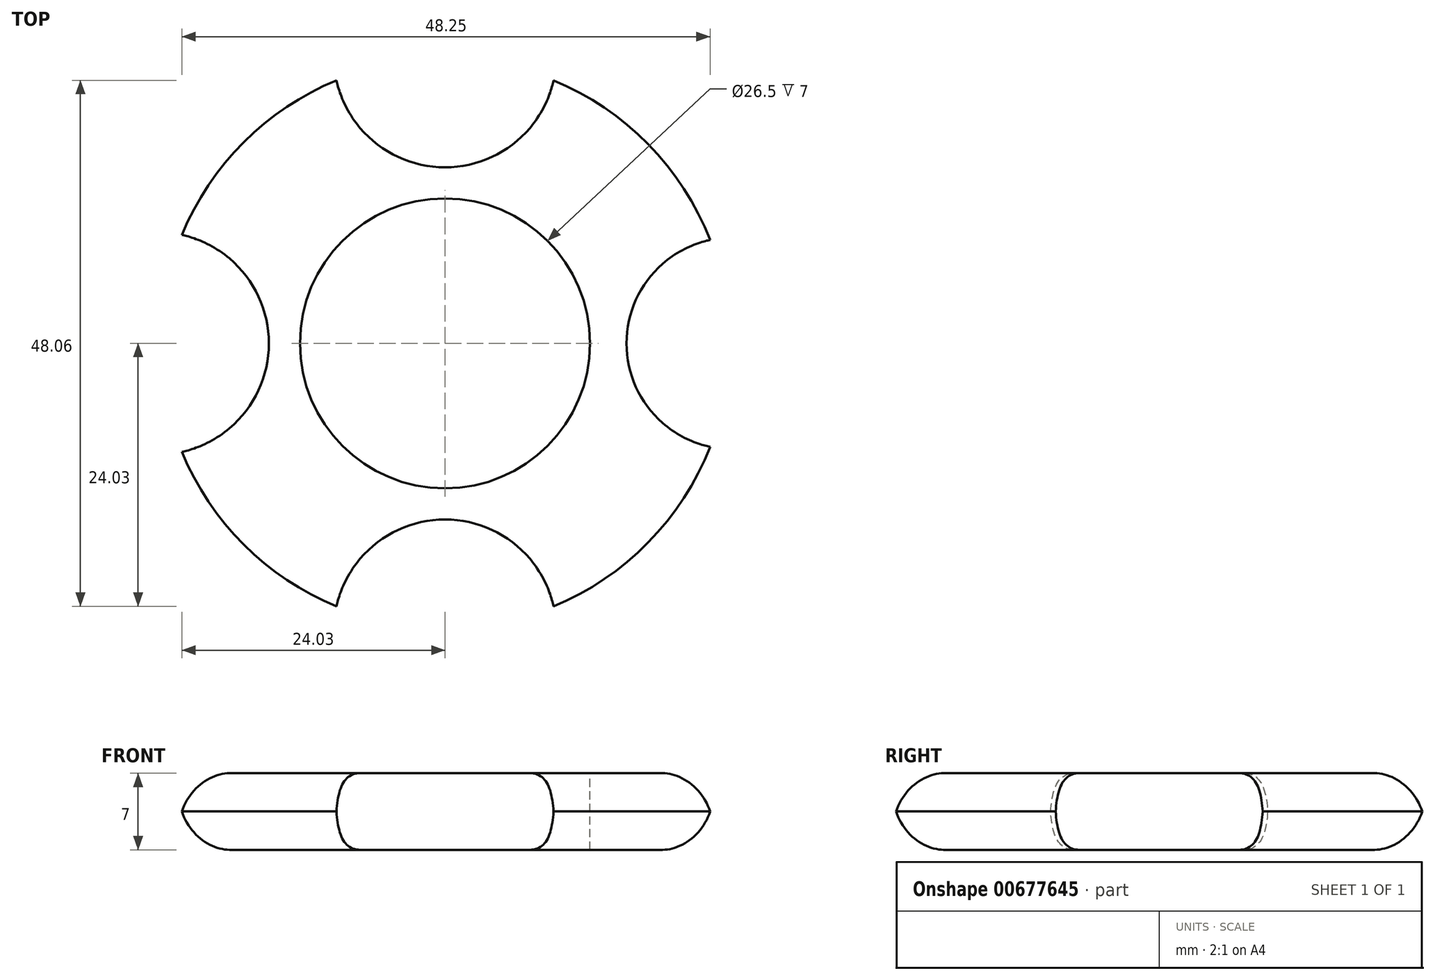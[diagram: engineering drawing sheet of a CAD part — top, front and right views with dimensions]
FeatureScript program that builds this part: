
annotation { "Feature Type Name" : "Feature", "Feature Type Description" : "" }
export const myFeature = defineFeature(function(context is Context, id is Id, definition is map)
    precondition{}
    {
        {
            var Q0;
            Q0=qCreatedBy(makeId("Top.planeOp"),FACE);
            var sketch = newSketch(context, id + "F0", { "sketchPlane" : qUnion([Q0])});
            skCircle(sketch, "E0", {"center": v(0, 0) * mm, "radius": 26.25 * mm});
            skSolve(sketch);
        }
        {
            var Q0;
            Q0=qSketchRegion(id+"F0",true);
            extrude(context, id + "F1", {"entities" : qUnion([Q0]), "depth" : 7 * mm, "offsetDistance" : 25.4 * mm});
        }
        {
            var Q0;
            Q0=makeQuery(id+"F1.opExtrude","CAP_FACE",FACE,{"disambiguationData":[OSD([sQuery(id+"F0.wireOp",EDGE,"E0")])],"isStart":false});
            var sketch = newSketch(context, id + "F2", { "sketchPlane" : qUnion([Q0])});
            skCircle(sketch, "E1", {"center": v(0, 0) * mm, "radius": 13.25 * mm});
            skSolve(sketch);
        }
        {
            var Q0;
            Q0=qSketchRegion(id+"F2",true);
            extrude(context, id + "F3", {"entities" : qUnion([Q0]), "operationType" : NewBodyOperationType.REMOVE, "oppositeDirection" : true, "depth" : 25.4 * mm, "offsetDistance" : 25.4 * mm});
        }
        {
            var Q0;
            Q0=makeQuery(id+"F1.opExtrude","CAP_FACE",FACE,{"disambiguationData":[OSD([sQuery(id+"F0.wireOp",EDGE,"E0")])],"isStart":false});
            var sketch = newSketch(context, id + "F4", { "sketchPlane" : qUnion([Q0])});
            skCircle(sketch, "E2", {"center": v(0, -26.25) * mm, "radius": 10.16 * mm});
            skCircle(sketch, "E3", {"center": v(-26.25, 0) * mm, "radius": 10.16 * mm});
            skCircle(sketch, "E4", {"center": v(0, 26.25) * mm, "radius": 10.16 * mm});
            skCircle(sketch, "E5", {"center": v(26.25, 0) * mm, "radius": 9.67 * mm});
            skSolve(sketch);
        }
        {
            var Q0;
            Q0=qSketchRegion(id+"F4",true);
            extrude(context, id + "F5", {"entities" : qUnion([Q0]), "operationType" : NewBodyOperationType.REMOVE, "oppositeDirection" : true, "depth" : 25.4 * mm, "offsetDistance" : 25.4 * mm});
        }
        {
            var Q0;
            {var subQ0=sQuery(id+"F0.wireOp",EDGE,"E0");Q0=makeQuery(id+"F5.boolean.opBoolean","SPLIT",EDGE,{"disambiguationData":[TD([makeQuery(id+"F1.opExtrude","SWEPT_FACE",FACE,{"disambiguationData":[OSD([subQ0])]}),makeQuery(id+"F1.opExtrude","CAP_FACE",FACE,{"disambiguationData":[OSD([subQ0])],"isStart":true}),makeQuery(id+"F5.opExtrude","SWEPT_FACE",FACE,{"disambiguationData":[OSD([sQuery(id+"F4.wireOp",EDGE,"E2")])]}),makeQuery(id+"F5.opExtrude","SWEPT_FACE",FACE,{"disambiguationData":[OSD([sQuery(id+"F4.wireOp",EDGE,"E5")])]})])],"derivedFrom":makeQuery(id+"F1.opExtrude","CAP_EDGE",EDGE,{"disambiguationData":[OSD([subQ0])],"isStart":true})});}
            var Q1;
            {var subQ0=sQuery(id+"F0.wireOp",EDGE,"E0");Q1=makeQuery(id+"F5.boolean.opBoolean","SPLIT",EDGE,{"disambiguationData":[TD([makeQuery(id+"F1.opExtrude","SWEPT_FACE",FACE,{"disambiguationData":[OSD([subQ0])]}),makeQuery(id+"F1.opExtrude","CAP_FACE",FACE,{"disambiguationData":[OSD([subQ0])],"isStart":true}),makeQuery(id+"F5.opExtrude","SWEPT_FACE",FACE,{"disambiguationData":[OSD([sQuery(id+"F4.wireOp",EDGE,"E2")])]}),makeQuery(id+"F5.opExtrude","SWEPT_FACE",FACE,{"disambiguationData":[OSD([sQuery(id+"F4.wireOp",EDGE,"E3")])]})])],"derivedFrom":makeQuery(id+"F1.opExtrude","CAP_EDGE",EDGE,{"disambiguationData":[OSD([subQ0])],"isStart":true})});}
            var Q2;
            {var subQ0=sQuery(id+"F0.wireOp",EDGE,"E0");Q2=makeQuery(id+"F5.boolean.opBoolean","SPLIT",EDGE,{"disambiguationData":[TD([makeQuery(id+"F1.opExtrude","SWEPT_FACE",FACE,{"disambiguationData":[OSD([subQ0])]}),makeQuery(id+"F1.opExtrude","CAP_FACE",FACE,{"disambiguationData":[OSD([subQ0])],"isStart":true}),makeQuery(id+"F5.opExtrude","SWEPT_FACE",FACE,{"disambiguationData":[OSD([sQuery(id+"F4.wireOp",EDGE,"E3")])]}),makeQuery(id+"F5.opExtrude","SWEPT_FACE",FACE,{"disambiguationData":[OSD([sQuery(id+"F4.wireOp",EDGE,"E4")])]})])],"derivedFrom":makeQuery(id+"F1.opExtrude","CAP_EDGE",EDGE,{"disambiguationData":[OSD([subQ0])],"isStart":true})});}
            var Q3;
            {var subQ0=sQuery(id+"F0.wireOp",EDGE,"E0");Q3=makeQuery(id+"F5.boolean.opBoolean","SPLIT",EDGE,{"disambiguationData":[TD([makeQuery(id+"F1.opExtrude","SWEPT_FACE",FACE,{"disambiguationData":[OSD([subQ0])]}),makeQuery(id+"F1.opExtrude","CAP_FACE",FACE,{"disambiguationData":[OSD([subQ0])],"isStart":false}),makeQuery(id+"F5.opExtrude","SWEPT_FACE",FACE,{"disambiguationData":[OSD([sQuery(id+"F4.wireOp",EDGE,"E3")])]}),makeQuery(id+"F5.opExtrude","SWEPT_FACE",FACE,{"disambiguationData":[OSD([sQuery(id+"F4.wireOp",EDGE,"E4")])]})])],"derivedFrom":makeQuery(id+"F1.opExtrude","CAP_EDGE",EDGE,{"disambiguationData":[OSD([subQ0])],"isStart":false})});}
            var Q4;
            {var subQ0=sQuery(id+"F0.wireOp",EDGE,"E0");Q4=makeQuery(id+"F5.boolean.opBoolean","SPLIT",EDGE,{"disambiguationData":[TD([makeQuery(id+"F1.opExtrude","SWEPT_FACE",FACE,{"disambiguationData":[OSD([subQ0])]}),makeQuery(id+"F1.opExtrude","CAP_FACE",FACE,{"disambiguationData":[OSD([subQ0])],"isStart":false}),makeQuery(id+"F5.opExtrude","SWEPT_FACE",FACE,{"disambiguationData":[OSD([sQuery(id+"F4.wireOp",EDGE,"E2")])]}),makeQuery(id+"F5.opExtrude","SWEPT_FACE",FACE,{"disambiguationData":[OSD([sQuery(id+"F4.wireOp",EDGE,"E3")])]})])],"derivedFrom":makeQuery(id+"F1.opExtrude","CAP_EDGE",EDGE,{"disambiguationData":[OSD([subQ0])],"isStart":false})});}
            var Q5;
            {var subQ0=sQuery(id+"F0.wireOp",EDGE,"E0");Q5=makeQuery(id+"F5.boolean.opBoolean","SPLIT",EDGE,{"disambiguationData":[TD([makeQuery(id+"F1.opExtrude","SWEPT_FACE",FACE,{"disambiguationData":[OSD([subQ0])]}),makeQuery(id+"F1.opExtrude","CAP_FACE",FACE,{"disambiguationData":[OSD([subQ0])],"isStart":false}),makeQuery(id+"F5.opExtrude","SWEPT_FACE",FACE,{"disambiguationData":[OSD([sQuery(id+"F4.wireOp",EDGE,"E2")])]}),makeQuery(id+"F5.opExtrude","SWEPT_FACE",FACE,{"disambiguationData":[OSD([sQuery(id+"F4.wireOp",EDGE,"E5")])]})])],"derivedFrom":makeQuery(id+"F1.opExtrude","CAP_EDGE",EDGE,{"disambiguationData":[OSD([subQ0])],"isStart":false})});}
            var Q6;
            {var subQ0=sQuery(id+"F0.wireOp",EDGE,"E0");Q6=makeQuery(id+"F5.boolean.opBoolean","SPLIT",EDGE,{"disambiguationData":[TD([makeQuery(id+"F1.opExtrude","SWEPT_FACE",FACE,{"disambiguationData":[OSD([subQ0])]}),makeQuery(id+"F1.opExtrude","CAP_FACE",FACE,{"disambiguationData":[OSD([subQ0])],"isStart":false}),makeQuery(id+"F5.opExtrude","SWEPT_FACE",FACE,{"disambiguationData":[OSD([sQuery(id+"F4.wireOp",EDGE,"E4")])]}),makeQuery(id+"F5.opExtrude","SWEPT_FACE",FACE,{"disambiguationData":[OSD([sQuery(id+"F4.wireOp",EDGE,"E5")])]})])],"derivedFrom":makeQuery(id+"F1.opExtrude","CAP_EDGE",EDGE,{"disambiguationData":[OSD([subQ0])],"isStart":false})});}
            var Q7;
            {var subQ0=sQuery(id+"F0.wireOp",EDGE,"E0");Q7=makeQuery(id+"F5.boolean.opBoolean","SPLIT",EDGE,{"disambiguationData":[TD([makeQuery(id+"F1.opExtrude","SWEPT_FACE",FACE,{"disambiguationData":[OSD([subQ0])]}),makeQuery(id+"F1.opExtrude","CAP_FACE",FACE,{"disambiguationData":[OSD([subQ0])],"isStart":true}),makeQuery(id+"F5.opExtrude","SWEPT_FACE",FACE,{"disambiguationData":[OSD([sQuery(id+"F4.wireOp",EDGE,"E4")])]}),makeQuery(id+"F5.opExtrude","SWEPT_FACE",FACE,{"disambiguationData":[OSD([sQuery(id+"F4.wireOp",EDGE,"E5")])]})])],"derivedFrom":makeQuery(id+"F1.opExtrude","CAP_EDGE",EDGE,{"disambiguationData":[OSD([subQ0])],"isStart":true})});}
            fillet(context, id + "F6", {"entities" : qUnion([Q0, Q1, Q2, Q3, Q4, Q5, Q6, Q7]), "radius" : 5.08 * mm, "tangentPropagation" : true, "allowEdgeOverflow" : false});
        }
    });
